# Revit family: МетеорЛифт_Пассажирский_МетеорЛифт_EvoMR
name_source: partatom
category: Оборудование
units: mm (PartAtom-declared; Revit-internal decimal feet)

## family parameters
Всегда вертикально = Да
Общий = Да
При загрузке вырезать с полостями = Да
Размер круглого соединителя = Использовать диаметр
Тип детали = Нормальный
Точка расчета площади = Нет

## types (5) — shared parameters
CAGOVLOC 1 = Нет
URL = https://meteor.ru
Изготовитель = ООО "Метеор Лифт"
Накладное = Объемная панель
Описание = Лифт электрический пассажирский с машинным помещением
РамаЛебедки = МетеорЛифт_РамаЛебедки_МетеорЛифт_EvoMR
РамаЛебедки_Отсутствует = МетеорЛифт_РамаЛебедки_Отсутствует
Телефон = +7 (495) 974-24-40
zero-valued in all types: Отметка по умолчанию

## per-type parameters (varying)
| type | CAGOVLOC | CAGOVLOC 2 | CAGOVLOC 3 | CAGOVLOC 4 | CD | CW | CWTLOC | CWTLOC_12 | CWTLOC_13 | DL | NBPAS | TCLOC | Ось подвески | Ось противовеса | Привязка отверстия для ПК | Привязка переднего фасада кабины | РамаЛебедки_12 | РамаЛебедки_13 | Расположение противовеса | Тип кабины | Штихмасс кабины |
| Г/п 1000 кг / Кабина 1600х1400 (ШхГ) | 3 | Нет | Да | Нет | 1400 мм | 1600 мм | 12 | Да | Нет | 1000 | 13 | 2 | 250 мм | 960 мм | 475 мм | 600 мм | МетеорЛифт_РамаЛебедки_МетеорЛифт_EvoMR | МетеорЛифт_РамаЛебедки_Отсутствует | Сзади | 13W | 1680 мм |
| Г/п 1000 кг / Кабина 2100х1100 (ШхГ) | 3 | Нет | Да | Нет | 1100 мм | 2100 мм | 12 | Да | Нет | 1000 | 13 | 2 | 250 мм | 797 мм | 450 мм | 480 мм | МетеорЛифт_РамаЛебедки_МетеорЛифт_EvoMR | МетеорЛифт_РамаЛебедки_Отсутствует | Сзади | 13X | 2180 мм |
| Г/п 400 кг / Кабина 1100х950 (ШхГ) | 2 | Да | Нет | Нет | 950 мм | 1100 мм | 12 | Да | Нет | 400 | 5 | 1 | 205 мм | 665 мм | 410 мм | 440 мм | МетеорЛифт_РамаЛебедки_МетеорЛифт_EvoMR | МетеорЛифт_РамаЛебедки_Отсутствует | Сзади | 05W | 1180 мм |
| Г/п 630 кг / Кабина 1100х1400 (ШхГ) | 2 | Да | Нет | Нет | 1400 мм | 1100 мм | 13 | Нет | Да | 630 | 8 | 2 | 205 мм | 777 мм | 710 мм | 600 мм | МетеорЛифт_РамаЛебедки_Отсутствует | МетеорЛифт_РамаЛебедки_МетеорЛифт_EvoMR | Сбоку | 08D | 1180 мм |
| Г/п 1000 кг / Кабина 1100х2100 (ШхГ) | 4 | Нет | Нет | Да | 2100 мм | 1100 мм | 13 | Нет | Да | 1000 | 13 | 3 | 250 мм | 771 мм | 750 мм | 920 мм | МетеорЛифт_РамаЛебедки_Отсутствует | МетеорЛифт_РамаЛебедки_МетеорЛифт_EvoMR | Сбоку | 13D | 1180 мм |

## geometry (parser evidence)
native form markers: Sweep x3
no freeform markers — native parametric forms only
